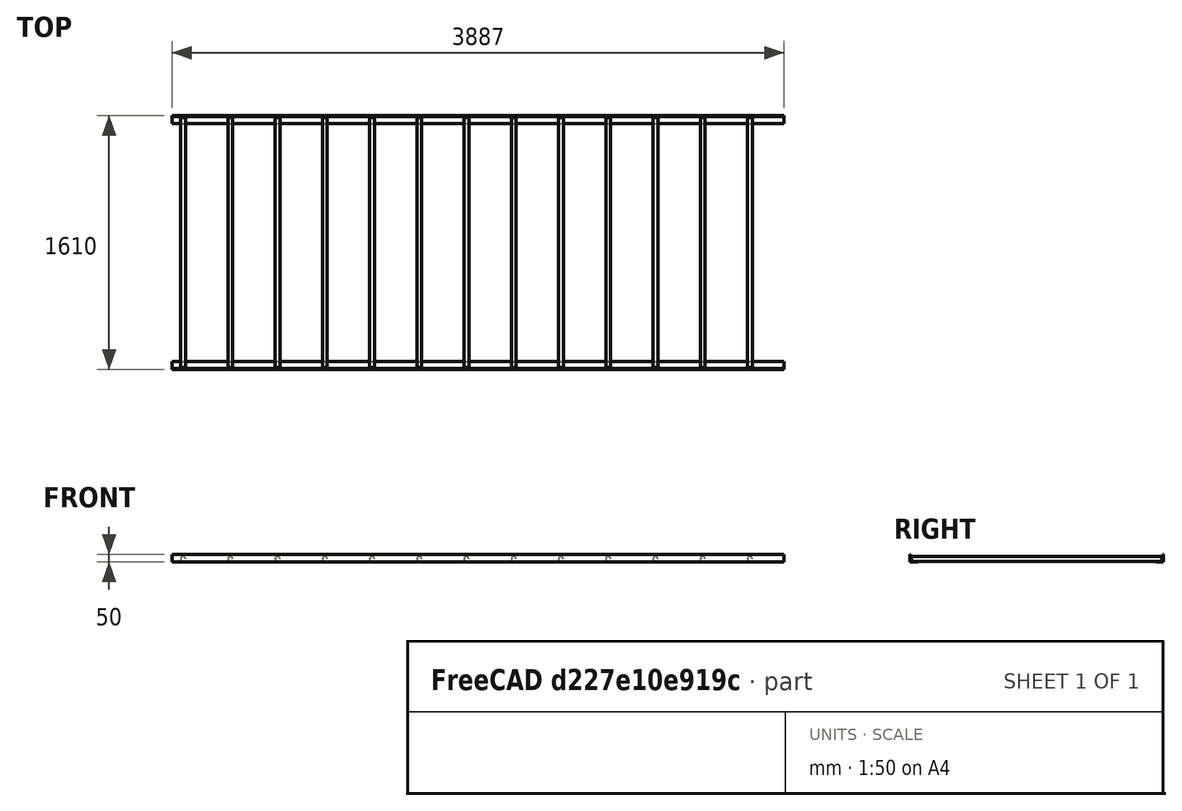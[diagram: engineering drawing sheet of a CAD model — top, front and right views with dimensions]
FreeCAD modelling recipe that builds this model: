
FCSTD DOCUMENT  (FreeCAD 0.18R16131 (Git))
Label: hrazda2
License: All rights reserved
LicenseURL: http://en.wikipedia.org/wiki/All_rights_reserved
objects: Part::Box×4, Part::Cut×2, App::Part×1, Part::Cylinder×1, Part::FeaturePython×1
note: 8 computed .brp shape members not serialized (recipe doc carries the construction recipe); baked Part::Feature solids carry a one-line shape summary decoded from their .brp

FEATURE [App::Part] Part
  Origin = -> Origin
FEATURE [Part::Box] Box  label="Cube"
  AttacherType = Attacher::AttachEngine3D
  Height = 50
  Length = 3887
  Width = 50
FEATURE [Part::Box] Box001  label="Cube001"
  AttacherType = Attacher::AttachEngine3D
  Height = 50
  Length = 3887
  Placement = pos=(0,4,4) rot=(0,0,1;0rad)
  Width = 50
FEATURE [Part::Cut] Cut
  Base = -> Box
  Tool = -> Box001
FEATURE [Part::Box] Box002  label="Cube002"
  AttacherType = Attacher::AttachEngine3D
  Height = 50
  Length = 3887
  Placement = pos=(0,1610,0) rot=(0,0,1;0rad)
  Width = 50
FEATURE [Part::Box] Box003  label="Cube003"
  AttacherType = Attacher::AttachEngine3D
  Height = 50
  Length = 3887
  Placement = pos=(0,1606,4) rot=(0,0,1;0rad)
  Width = 50
FEATURE [Part::Cut] Cut001
  Base = -> Box002
  Placement = pos=(0,-50,0) rot=(0,0,1;0rad)
  Tool = -> Box003
FEATURE [Part::Cylinder] Cylinder
  Angle = 360
  AttacherType = Attacher::AttachEngine3D
  Height = 1590
  Placement = pos=(70,10,20) rot=(-1,0,0;1.5708rad)
  Radius = 15
FEATURE [Part::FeaturePython] Array  # Draft array (typed FeaturePython)
  Angle = 360
  ArrayType = 0
  Axis = (0,0,1)
  Base = -> Cylinder
  Center = (0,0,0)
  Fuse = false
  IntervalAxis = (1000,0,0)
  IntervalX = (300,0,0)
  IntervalY = (0,1,0)
  IntervalZ = (0,0,1)
  NumberPolar = 1
  NumberX = 13
  NumberY = 1
  NumberZ = 1
